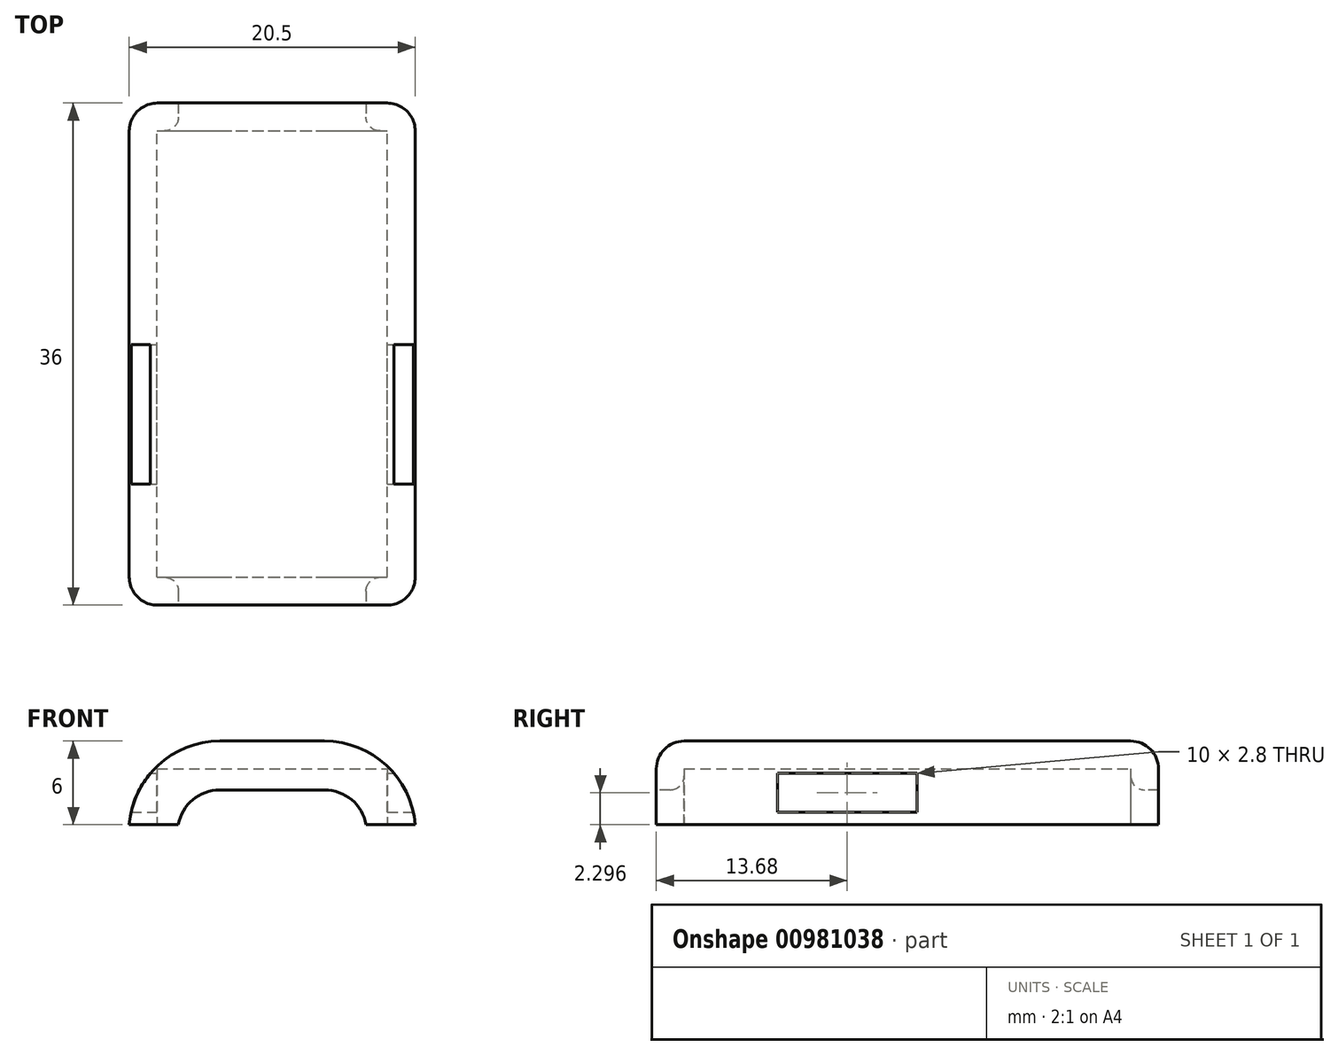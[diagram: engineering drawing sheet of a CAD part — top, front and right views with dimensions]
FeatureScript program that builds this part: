
annotation { "Feature Type Name" : "Feature", "Feature Type Description" : "" }
export const myFeature = defineFeature(function(context is Context, id is Id, definition is map)
    precondition{}
    {
        {
            var Q0;
            Q0=qCreatedBy(makeId("Top.planeOp"),FACE);
            var sketch = newSketch(context, id + "F0", { "sketchPlane" : qUnion([Q0])});
            skLineSegment(sketch, "E0.bottom", {"start": v(-8.14, -16.68) * mm, "end": v(8.36, -16.68) * mm});
            skLineSegment(sketch, "E0.top", {"start": v(-8.14, 15.32) * mm, "end": v(8.36, 15.32) * mm});
            skLineSegment(sketch, "E0.left", {"start": v(-8.14, -16.68) * mm, "end": v(-8.14, 15.32) * mm});
            skLineSegment(sketch, "E0.right", {"start": v(8.36, -16.68) * mm, "end": v(8.36, 15.32) * mm});
            skSolve(sketch);
        }
        {
            var Q0;
            Q0=qCreatedBy(makeId("Top.planeOp"),FACE);
            var sketch = newSketch(context, id + "F1", { "sketchPlane" : qUnion([Q0])});
            skLineSegment(sketch, "E1.0", {"start": v(-10.14, -18.68) * mm, "end": v(-10.14, 17.32) * mm});
            skLineSegment(sketch, "E2.0", {"start": v(-10.14, 17.32) * mm, "end": v(10.36, 17.32) * mm});
            skLineSegment(sketch, "E3.0", {"start": v(10.36, -18.68) * mm, "end": v(10.36, 17.32) * mm});
            skLineSegment(sketch, "E4.0", {"start": v(-10.14, -18.68) * mm, "end": v(10.36, -18.68) * mm});
            skSolve(sketch);
        }
        {
            var Q0;
            Q0=makeQuery(id+"F1.imprint","IMPRINT",FACE,{"disambiguationData":[TD([[makeQuery(id+"F1.imprint","IMPRINT",EDGE,{"derivedFrom":sQuery(id+"F1.wireOp",EDGE,"E1.0")}),-1.0]])]});
            extrude(context, id + "F2", {"entities" : qUnion([Q0]), "depth" : 6 * mm, "offsetDistance" : 25 * mm});
        }
        {
            var Q0;
            Q0=makeQuery(id+"F0.imprint","IMPRINT",FACE,{"disambiguationData":[TD([[makeQuery(id+"F0.imprint","IMPRINT",EDGE,{"derivedFrom":sQuery(id+"F0.wireOp",EDGE,"E0.bottom")}),1.0]])]});
            extrude(context, id + "F3", {"entities" : qUnion([Q0]), "operationType" : NewBodyOperationType.REMOVE, "depth" : 4 * mm, "offsetDistance" : 25 * mm});
        }
        {
            var Q0;
            Q0=makeQuery(id+"F2.opExtrude","CAP_EDGE",EDGE,{"disambiguationData":[OSD([sQuery(id+"F1.wireOp",EDGE,"E3.0")])],"isStart":false});
            var Q1;
            Q1=makeQuery(id+"F2.opExtrude","CAP_EDGE",EDGE,{"disambiguationData":[OSD([sQuery(id+"F1.wireOp",EDGE,"E1.0")])],"isStart":false});
            fillet(context, id + "F4", {"entities" : qUnion([Q0, Q1]), "radius" : 6.52 * mm, "tangentPropagation" : true, "allowEdgeOverflow" : false});
        }
        {
            var Q0;
            Q0=makeQuery(id+"F2.opExtrude","CAP_EDGE",EDGE,{"disambiguationData":[OSD([sQuery(id+"F1.wireOp",EDGE,"E2.0")])],"isStart":false});
            var Q1;
            Q1=makeQuery(id+"F4.opFillet","BLEND_EDGE",EDGE,{"blendedFrom":[makeQuery(id+"F2.opExtrude","CAP_EDGE",EDGE,{"disambiguationData":[OSD([sQuery(id+"F1.wireOp",EDGE,"E3.0")])],"isStart":false}),makeQuery(id+"F2.opExtrude","SWEPT_FACE",FACE,{"disambiguationData":[OSD([sQuery(id+"F1.wireOp",EDGE,"E2.0")])]})],"blendedInto":[makeQuery(id+"F2.opExtrude","SWEPT_FACE",FACE,{"disambiguationData":[OSD([sQuery(id+"F1.wireOp",EDGE,"E2.0")])]})]});
            var Q2;
            Q2=makeQuery(id+"F4.opFillet","BLEND_EDGE",EDGE,{"blendedFrom":[makeQuery(id+"F2.opExtrude","CAP_EDGE",EDGE,{"disambiguationData":[OSD([sQuery(id+"F1.wireOp",EDGE,"E1.0")])],"isStart":false}),makeQuery(id+"F2.opExtrude","SWEPT_FACE",FACE,{"disambiguationData":[OSD([sQuery(id+"F1.wireOp",EDGE,"E4.0")])]})],"blendedInto":[makeQuery(id+"F2.opExtrude","SWEPT_FACE",FACE,{"disambiguationData":[OSD([sQuery(id+"F1.wireOp",EDGE,"E4.0")])]})]});
            fillet(context, id + "F5", {"entities" : qUnion([Q0, Q1, Q2]), "radius" : 2 * mm, "tangentPropagation" : true, "allowEdgeOverflow" : false});
        }
        {
            var Q0;
            Q0=qCreatedBy(makeId("Front.planeOp"),FACE);
            var sketch = newSketch(context, id + "F6", { "sketchPlane" : qUnion([Q0])});
            skArc(sketch, "E5.0", {"start": v(3.86, 2.5) * mm, "mid": v(5.8, 1.8) * mm, "end": v(6.84, 0) * mm});
            skArc(sketch, "E6.0", {"start": v(-6.62, 0) * mm, "mid": v(-5.58, 1.8) * mm, "end": v(-3.64, 2.5) * mm});
            skLineSegment(sketch, "E7", {"start": v(6.84, 0) * mm, "end": v(-6.62, 0) * mm});
            skLineSegment(sketch, "E8", {"start": v(3.86, 2.5) * mm, "end": v(-3.64, 2.5) * mm});
            skSolve(sketch);
        }
        {
            var Q0;
            Q0 = qSketchRegion(id + "F6", true);
            extrude(context, id + "F7", {"entities" : qUnion([Q0]), "operationType" : NewBodyOperationType.REMOVE, "oppositeDirection" : true, "depth" : 25 * mm, "offsetDistance" : 25 * mm, "hasSecondDirection" : true, "secondDirectionOppositeDirection" : false, "secondDirectionDepth" : 20.4 * mm});
        }
        {
            var Q0;
            Q0=makeQuery(id+"F7.boolean.opBoolean","INTERSECT",EDGE,{"derivedFrom":[makeQuery(id+"F3.boolean.opBoolean","COPY",FACE,{"derivedFrom":makeQuery(id+"F3.opExtrude","SWEPT_FACE",FACE,{"disambiguationData":[OSD([sQuery(id+"F0.wireOp",EDGE,"E0.top")])]})}),makeQuery(id+"F7.opExtrude","SWEPT_FACE",FACE,{"disambiguationData":[OSD([sQuery(id+"F6.wireOp",EDGE,"E6.0")])]})]});
            var Q1;
            Q1=makeQuery(id+"F7.boolean.opBoolean","INTERSECT",EDGE,{"derivedFrom":[makeQuery(id+"F3.boolean.opBoolean","COPY",FACE,{"derivedFrom":makeQuery(id+"F3.opExtrude","SWEPT_FACE",FACE,{"disambiguationData":[OSD([sQuery(id+"F0.wireOp",EDGE,"E0.bottom")])]})}),makeQuery(id+"F7.opExtrude","SWEPT_FACE",FACE,{"disambiguationData":[OSD([sQuery(id+"F6.wireOp",EDGE,"E8")])]})]});
            fillet(context, id + "F8", {"entities" : qUnion([Q0, Q1]), "radius" : 1 * mm, "tangentPropagation" : true, "allowEdgeOverflow" : false});
        }
        {
            var Q0;
            Q0=qCreatedBy(makeId("Right.planeOp"),FACE);
            var sketch = newSketch(context, id + "F9", { "sketchPlane" : qUnion([Q0])});
            skLineSegment(sketch, "E9.bottom", {"start": v(0, 3.7) * mm, "end": v(-10, 3.7) * mm});
            skLineSegment(sketch, "E9.top", {"start": v(0, 0.9) * mm, "end": v(-10, 0.9) * mm});
            skLineSegment(sketch, "E9.left", {"start": v(0, 3.7) * mm, "end": v(0, 0.9) * mm});
            skLineSegment(sketch, "E9.right", {"start": v(-10, 3.7) * mm, "end": v(-10, 0.9) * mm});
            skSolve(sketch);
        }
        {
            var Q0;
            Q0 = qSketchRegion(id + "F9", true);
            extrude(context, id + "F10", {"entities" : qUnion([Q0]), "operationType" : NewBodyOperationType.REMOVE, "oppositeDirection" : true, "depth" : 25 * mm, "offsetDistance" : 25 * mm, "hasSecondDirection" : true, "secondDirectionOppositeDirection" : false, "secondDirectionDepth" : 25 * mm});
        }
    });
